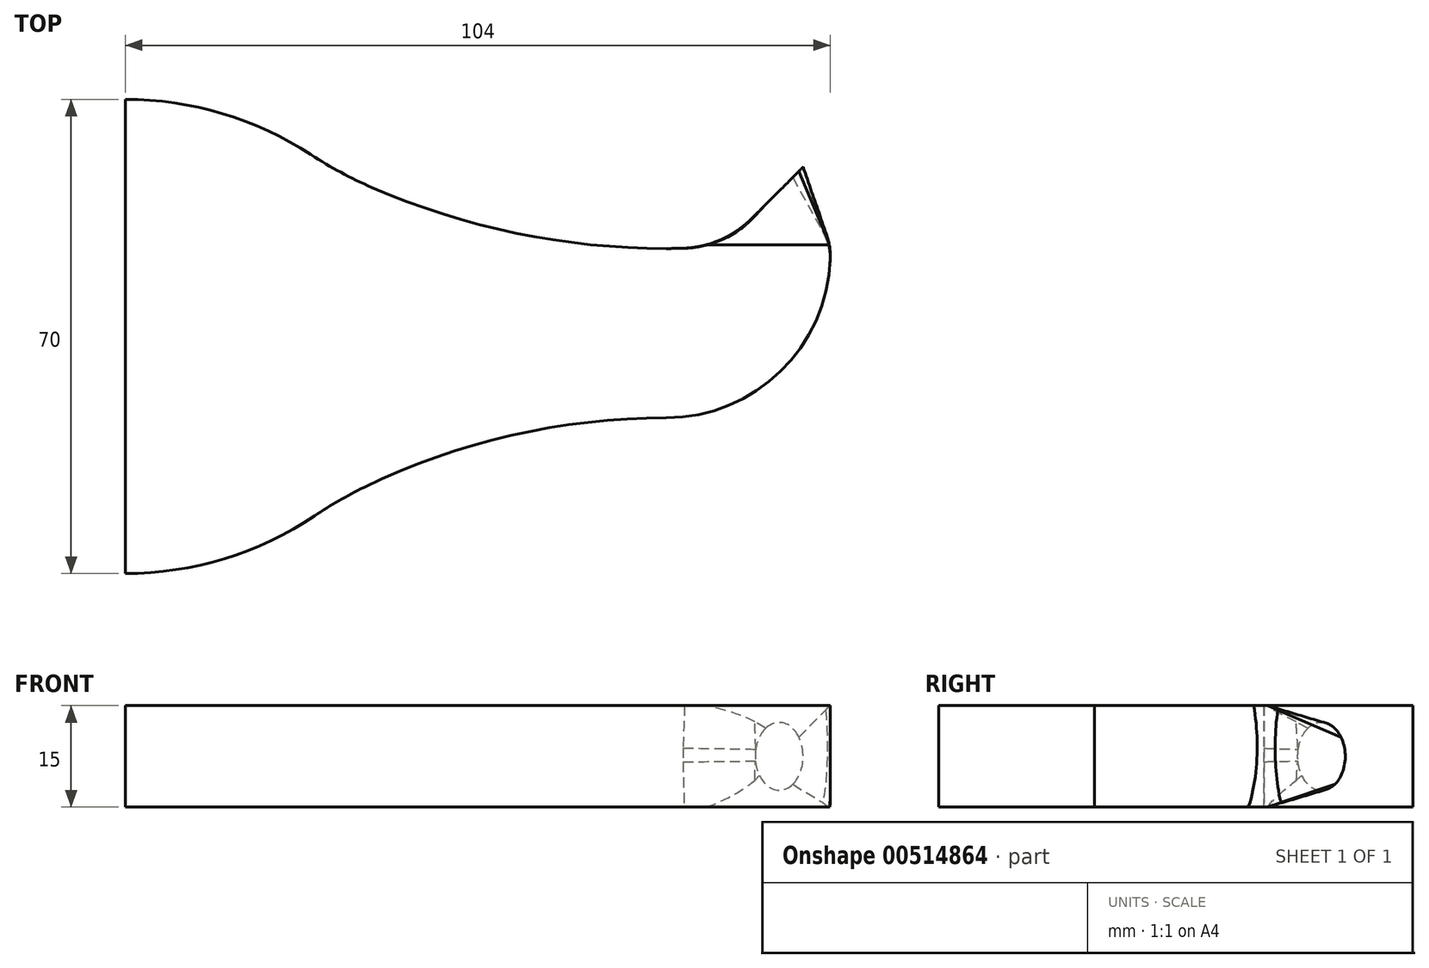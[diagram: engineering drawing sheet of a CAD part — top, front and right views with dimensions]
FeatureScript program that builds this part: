
annotation { "Feature Type Name" : "Feature", "Feature Type Description" : "" }
export const myFeature = defineFeature(function(context is Context, id is Id, definition is map)
    precondition{}
    {
        {
            var Q0;
            Q0=qCreatedBy(makeId("Top.planeOp"),FACE);
            var sketch = newSketch(context, id + "F0", { "sketchPlane" : qUnion([Q0])});
            skLineSegment(sketch, "E0.left", {"start": v(-50, 50) * mm, "end": v(-50, -50) * mm});
            skPoint(sketch, "E0.middle", {"position": v(0, 0) * mm});
            skLineSegment(sketch, "E1", {"start": v(-50, 50) * mm, "end": v(-50, 40) * mm});
            skLineSegment(sketch, "E2", {"start": v(50, 40) * mm, "end": v(42.93, 32.93) * mm});
            skLineSegment(sketch, "E3", {"start": v(42.93, 32.93) * mm, "end": v(46.46, 36.46) * mm});
            skLineSegment(sketch, "E4", {"start": v(-50, 0) * mm, "end": v(-50, -10) * mm});
            skLineSegment(sketch, "E5", {"start": v(-50, -10) * mm, "end": v(-50, 15) * mm});
            skLineSegment(sketch, "E6", {"start": v(-50, 15) * mm, "end": v(114.78, 15) * mm});
            skLineSegment(sketch, "E7", {"start": v(42.93, 32.93) * mm, "end": v(42.93, -37.04) * mm});
            skLineSegment(sketch, "E8", {"start": v(-50, 15) * mm, "end": v(30, 15) * mm});
            skLineSegment(sketch, "E9", {"start": v(30, 15) * mm, "end": v(30, 30) * mm});
            skLineSegment(sketch, "E10", {"start": v(30, 15) * mm, "end": v(30, 0) * mm});
            skLineSegment(sketch, "E11", {"start": v(42.93, 32.93) * mm, "end": v(81, 32.93) * mm});
            skLineSegment(sketch, "E12", {"start": v(46.46, 36.46) * mm, "end": v(46.46, 32.93) * mm});
            skLineSegment(sketch, "E13", {"start": v(46.46, 36.46) * mm, "end": v(46.46, 0) * mm});
            skLineSegment(sketch, "E14", {"start": v(46.46, 36.46) * mm, "end": v(62.14, 20.79) * mm});
            skLineSegment(sketch, "E15", {"start": v(-50, 50) * mm, "end": v(-109.66, 50) * mm});
            skLineSegment(sketch, "E16", {"start": v(-50, 40) * mm, "end": v(-110.5, 40) * mm});
            skLineSegment(sketch, "E17", {"start": v(-50, 15) * mm, "end": v(-113.83, 15) * mm});
            skLineSegment(sketch, "E18", {"start": v(-50, 0) * mm, "end": v(-113, 0) * mm});
            skLineSegment(sketch, "E19", {"start": v(-50, -10) * mm, "end": v(-113, -10) * mm});
            skLineSegment(sketch, "E20", {"start": v(-50, -50) * mm, "end": v(-111.33, -50) * mm});
            skLineSegment(sketch, "E21", {"start": v(30, 30) * mm, "end": v(95.7, 30) * mm});
            skPoint(sketch, "E22", {"position": v(42.93, 30) * mm});
            skPoint(sketch, "E23", {"position": v(46.46, 30) * mm});
            skPoint(sketch, "E24", {"position": v(42.93, 28.5) * mm});
            skLineSegment(sketch, "E25", {"start": v(30, 15) * mm, "end": v(30, 7.5) * mm});
            skLineSegment(sketch, "E26", {"start": v(30, 15) * mm, "end": v(30, 22.5) * mm});
            skLineSegment(sketch, "E27", {"start": v(30, 15) * mm, "end": v(0, 15) * mm});
            skLineSegment(sketch, "E28", {"start": v(-50, 15) * mm, "end": v(-30, 15) * mm});
            skLineSegment(sketch, "E29", {"start": v(-30, 15) * mm, "end": v(-10, 15) * mm});
            skLineSegment(sketch, "E30", {"start": v(-10, 15) * mm, "end": v(10, 15) * mm});
            skLineSegment(sketch, "E31", {"start": v(30, 30) * mm, "end": v(-50, 30) * mm});
            skLineSegment(sketch, "E32", {"start": v(-50, 40) * mm, "end": v(50, 40) * mm});
            skSolve(sketch);
        }
        {
            var Q0;
            Q0=sQuery(id+"F0.wireOp",EDGE,"E2");
            cPlane(context, id + "F1", {"entities" : qUnion([Q0]), "cplaneType" : CPlaneType.LINE_ANGLE, "offset" : 25 * mm, "angle" : 90 * degree, "width" : 150 * mm, "height" : 150 * mm});
        }
        {
            var Q0;
            Q0=qCreatedBy(id+"F1.planeOp",FACE);
            var sketch = newSketch(context, id + "F2", { "sketchPlane" : qUnion([Q0])});
            skCircle(sketch, "E33", {"center": v(58.64, 0) * mm, "radius": 5 * mm});
            skSolve(sketch);
        }
        {
            var Q0;
            Q0=sQuery(id+"F0.wireOp",VERTEX,"E6.start");
            var Q1;
            Q1=qCreatedBy(makeId("Right.planeOp"),FACE);
            cPlane(context, id + "F3", {"entities" : qUnion([Q0, Q1]), "cplaneType" : CPlaneType.PLANE_POINT, "offset" : 25 * mm, "width" : 150 * mm, "height" : 150 * mm});
        }
        {
            var Q0;
            Q0=qCreatedBy(id+"F3.planeOp",FACE);
            var sketch = newSketch(context, id + "F4", { "sketchPlane" : qUnion([Q0])});
            skPoint(sketch, "E34", {"position": v(15, 0) * mm});
            skLineSegment(sketch, "E35", {"start": v(50, 10) * mm, "end": v(-20, 10) * mm});
            skLineSegment(sketch, "E36", {"start": v(50, -10) * mm, "end": v(-20, -10) * mm});
            skLineSegment(sketch, "E37", {"start": v(50, 10) * mm, "end": v(50, -10) * mm});
            skLineSegment(sketch, "E38", {"start": v(-20, 10) * mm, "end": v(-20, -10) * mm});
            skPoint(sketch, "E39", {"position": v(-50, 0) * mm});
            skPoint(sketch, "E40", {"position": v(50, 0) * mm});
            skPoint(sketch, "E41", {"position": v(-20, 0) * mm});
            skLineSegment(sketch, "E42", {"start": v(50, 0) * mm, "end": v(40, 0) * mm});
            skSolve(sketch);
        }
        {
            var Q0;
            Q0=qCreatedBy(makeId("Front.planeOp"),FACE);
            var Q1;
            Q1=sQuery(id+"F0.wireOp",VERTEX,"E24");
            cPlane(context, id + "F5", {"entities" : qUnion([Q0, Q1]), "cplaneType" : CPlaneType.PLANE_POINT, "offset" : 25 * mm, "width" : 150 * mm, "height" : 150 * mm});
        }
        {
            var Q0;
            Q0=qCreatedBy(id+"F5.planeOp",FACE);
            var sketch = newSketch(context, id + "F6", { "sketchPlane" : qUnion([Q0])});
            skPoint(sketch, "E43", {"position": v(46.46, 0) * mm});
            skLineSegment(sketch, "E44.bottom", {"start": v(38.96, -7.5) * mm, "end": v(53.96, -7.5) * mm});
            skLineSegment(sketch, "E44.top", {"start": v(38.96, 7.5) * mm, "end": v(53.96, 7.5) * mm});
            skLineSegment(sketch, "E44.left", {"start": v(38.96, -7.5) * mm, "end": v(38.96, 7.5) * mm});
            skLineSegment(sketch, "E44.right", {"start": v(53.96, -7.5) * mm, "end": v(53.96, 7.5) * mm});
            skPoint(sketch, "E45", {"position": v(38.96, 0) * mm});
            skPoint(sketch, "E46", {"position": v(53.96, 0) * mm});
            skSolve(sketch);
        }
        {
            var Q0;
            Q0=qCreatedBy(makeId("Top.planeOp"),FACE);
            var Q1;
            Q1=sQuery(id+"F6.wireOp",VERTEX,"E43");
            cPlane(context, id + "F7", {"entities" : qUnion([Q0, Q1]), "cplaneType" : CPlaneType.PLANE_POINT, "offset" : 25 * mm, "width" : 150 * mm, "height" : 150 * mm});
        }
        {
            var Q0;
            Q0=qCreatedBy(id+"F7.planeOp",FACE);
            var sketch = newSketch(context, id + "F8", { "sketchPlane" : qUnion([Q0])});
            skPoint(sketch, "E47", {"position": v(29.78, 27.97) * mm});
            skPoint(sketch, "E48", {"position": v(29.78, 2.97) * mm});
            skLineSegment(sketch, "E49", {"start": v(29.78, 27.97) * mm, "end": v(29.78, 2.97) * mm});
            skLineSegment(sketch, "E50", {"start": v(29.78, 27.97) * mm, "end": v(25.89, 27.97) * mm});
            skLineSegment(sketch, "E51", {"start": v(29.78, 2.97) * mm, "end": v(25.8, 2.97) * mm});
            skPoint(sketch, "E52", {"position": v(29.78, 15.47) * mm});
            skPoint(sketch, "E53", {"position": v(38.96, 28.5) * mm});
            skPoint(sketch, "E54", {"position": v(53.96, 28.5) * mm});
            skArc(sketch, "E55", {"start": v(29.78, 27.97) * mm, "mid": v(34.38, 28.1) * mm, "end": v(38.96, 28.5) * mm});
            skArc(sketch, "E56", {"start": v(29.78, 2.97) * mm, "mid": v(47.36, 10.54) * mm, "end": v(53.96, 28.5) * mm});
            skLineSegment(sketch, "E57", {"start": v(38.96, 28.5) * mm, "end": v(53.96, 28.5) * mm});
            skLineSegment(sketch, "E58", {"start": v(29.78, 15.47) * mm, "end": v(-60.44, 15.47) * mm});
            skSolve(sketch);
        }
        {
            var Q0;
            Q0=qCreatedBy(makeId("Top.planeOp"),FACE);
            var sketch = newSketch(context, id + "F9", { "sketchPlane" : qUnion([Q0])});
            skLineSegment(sketch, "E59", {"start": v(-20, 40) * mm, "end": v(-20, 40) * mm});
            skPoint(sketch, "E60", {"position": v(-50, -50) * mm});
            skPoint(sketch, "E61", {"position": v(29.78, 2.97) * mm});
            skPoint(sketch, "E62", {"position": v(29.78, 27.97) * mm});
            skLineSegment(sketch, "E63", {"start": v(29.78, 27.97) * mm, "end": v(24.78, 27.97) * mm});
            skLineSegment(sketch, "E64", {"start": v(29.78, 2.97) * mm, "end": v(24.78, 2.97) * mm});
            skArc(sketch, "E65", {"start": v(-20, 40) * mm, "mid": v(4.18, 31.02) * mm, "end": v(29.78, 27.97) * mm});
            skLineSegment(sketch, "E66", {"start": v(29.78, 27.97) * mm, "end": v(29.78, 2.97) * mm});
            skLineSegment(sketch, "E67", {"start": v(29.78, 15.47) * mm, "end": v(16.82, 15.47) * mm});
            skPoint(sketch, "E68", {"position": v(-50, 50) * mm});
            skPoint(sketch, "E69", {"position": v(-50, -20) * mm});
            skPoint(sketch, "E70", {"position": v(-50, 15.47) * mm});
            skLineSegment(sketch, "E71", {"start": v(-50, 50) * mm, "end": v(-50, -20) * mm});
            skLineSegment(sketch, "E72", {"start": v(-50, 50) * mm, "end": v(-61.71, 50) * mm});
            skArc(sketch, "E73", {"start": v(-20, 40) * mm, "mid": v(-34.19, 47.43) * mm, "end": v(-50, 50) * mm});
            skArc(sketch, "E74.MirrorCS", {"start": v(-20, -10) * mm, "mid": v(-34.19, -17.43) * mm, "end": v(-50, -20) * mm});
            skLineSegment(sketch, "E75", {"start": v(29.78, 2.97) * mm, "end": v(35.09, 2.97) * mm});
            skArc(sketch, "E76", {"start": v(29.78, 2.97) * mm, "mid": v(4.06, -0.32) * mm, "end": v(-20, -10) * mm});
            skSolve(sketch);
        }
        {
            var Q0;
            Q0=makeQuery(id+"F2.imprint","IMPRINT",FACE,{"disambiguationData":[TD([[makeQuery(id+"F2.imprint","IMPRINT",EDGE,{"derivedFrom":sQuery(id+"F2.wireOp",EDGE,"E33")}),1.0]])]});
            var Q1;
            Q1=makeQuery(id+"F6.imprint","IMPRINT",FACE,{"disambiguationData":[TD([[makeQuery(id+"F6.imprint","IMPRINT",EDGE,{"derivedFrom":sQuery(id+"F6.wireOp",EDGE,"E44.bottom")}),1.0]])]});
            loft(context, id + "F10", {"sheetProfilesArray" : [{ "sheetProfileEntities" : qUnion([Q0]) }, { "sheetProfileEntities" : qUnion([Q1]) }]});
        }
        {
            var Q0;
            {var subQ1=sQuery(id+"F9.wireOp",EDGE,"E65");Q0=makeQuery(id+"F9.imprint","IMPRINT",FACE,{"disambiguationData":[TD([[makeQuery(id+"F9.imprint","IMPRINT",EDGE,{"derivedFrom":subQ1}),-1.0]])]});}
            extrude(context, id + "F11", {"entities" : qUnion([Q0]), "operationType" : NewBodyOperationType.ADD, "endBound" : BoundingType.SYMMETRIC, "depth" : 15 * mm, "offsetDistance" : 25 * mm});
        }
        {
            var Q0;
            Q0=makeQuery(id+"F8.imprint","IMPRINT",FACE,{"disambiguationData":[TD([[makeQuery(id+"F8.imprint","IMPRINT",EDGE,{"derivedFrom":sQuery(id+"F8.wireOp",EDGE,"E49")}),1.0]])]});
            extrude(context, id + "F12", {"entities" : qUnion([Q0]), "operationType" : NewBodyOperationType.ADD, "endBound" : BoundingType.SYMMETRIC, "depth" : 15 * mm, "offsetDistance" : 25 * mm});
        }
        {
            var Q0;
            Q0=makeQuery(id+"F12.boolean.opBoolean","MERGE",EDGE,{"derivedFrom":[makeQuery(id+"F10.opLoft","MID_CAP_EDGE",EDGE,{"disambiguationData":[OSD([sQuery(id+"F6.wireOp",EDGE,"E44.bottom"),sQuery(id+"F6.wireOp",EDGE,"E44.top"),sQuery(id+"F6.wireOp",EDGE,"E44.left")])],"capPos":1.0}),makeQuery(id+"F12.opExtrude","SWEPT_EDGE",EDGE,{"disambiguationData":[OSD([sQuery(id+"F8.wireOp",EDGE,"E55"),sQuery(id+"F8.wireOp",EDGE,"E57")])]})]});
            fillet(context, id + "F13", {"entities" : qUnion([Q0]), "radius" : 15 * mm, "tangentPropagation" : true, "allowEdgeOverflow" : false});
        }
        {
            var Q0;
            Q0=makeQuery(id+"F12.boolean.opBoolean","MERGE",EDGE,{"derivedFrom":[makeQuery(id+"F10.opLoft","MID_CAP_EDGE",EDGE,{"disambiguationData":[OSD([sQuery(id+"F6.wireOp",EDGE,"E44.bottom"),sQuery(id+"F6.wireOp",EDGE,"E44.top"),sQuery(id+"F6.wireOp",EDGE,"E44.right")])],"capPos":1.0}),makeQuery(id+"F12.opExtrude","SWEPT_EDGE",EDGE,{"disambiguationData":[OSD([sQuery(id+"F8.wireOp",EDGE,"E56"),sQuery(id+"F8.wireOp",EDGE,"E57")])]})]});
            fillet(context, id + "F14", {"entities" : qUnion([Q0]), "radius" : 8 * mm, "tangentPropagation" : true, "allowEdgeOverflow" : false});
        }
        {
            var Q0;
            Q0=makeQuery(id+"F11.opExtrude","SWEPT_EDGE",EDGE,{"disambiguationData":[OSD([sQuery(id+"F9.wireOp",EDGE,"E65"),sQuery(id+"F9.wireOp",EDGE,"E73")])]});
            fillet(context, id + "F15", {"entities" : qUnion([Q0]), "radius" : 60 * mm, "tangentPropagation" : true, "allowEdgeOverflow" : false});
        }
        {
            var Q0;
            Q0=makeQuery(id+"F11.opExtrude","SWEPT_EDGE",EDGE,{"disambiguationData":[OSD([sQuery(id+"F9.wireOp",EDGE,"E74.MirrorCS"),sQuery(id+"F9.wireOp",EDGE,"E76")])]});
            fillet(context, id + "F16", {"entities" : qUnion([Q0]), "radius" : 60 * mm, "tangentPropagation" : true, "allowEdgeOverflow" : false});
        }
        {
            var Q0;
            Q0=qCreatedBy(makeId("Right.planeOp"),FACE);
            var Q1;
            Q1=sQuery(id+"F4.wireOp",VERTEX,"E34");
            cPlane(context, id + "F17", {"entities" : qUnion([Q0, Q1]), "cplaneType" : CPlaneType.PLANE_POINT, "offset" : 25 * mm, "width" : 150 * mm, "height" : 150 * mm});
        }
        {
            var Q0;
            Q0=qCreatedBy(id+"F1.planeOp",FACE);
            var Q1;
            Q1=sQuery(id+"F2.wireOp",VERTEX,"E33.center");
            cPlane(context, id + "F18", {"entities" : qUnion([Q0, Q1]), "cplaneType" : CPlaneType.PLANE_POINT, "offset" : 25 * mm, "width" : 150 * mm, "height" : 150 * mm});
        }
        {
            var Q0;
            Q0=qCreatedBy(id+"F18.planeOp",FACE);
            var sketch = newSketch(context, id + "F19", { "sketchPlane" : qUnion([Q0])});
            skCircle(sketch, "E77", {"center": v(58.64, 0) * mm, "radius": 5 * mm});
            skPoint(sketch, "E78", {"position": v(63.64, 0) * mm});
            skSolve(sketch);
        }
        {
            var Q0;
            Q0=sQuery(id+"F0.wireOp",VERTEX,"E27.end");
            var Q1;
            Q1=qCreatedBy(makeId("Top.planeOp"),FACE);
            cPlane(context, id + "F20", {"entities" : qUnion([Q0, Q1]), "cplaneType" : CPlaneType.PLANE_POINT, "offset" : 25 * mm, "width" : 150 * mm, "height" : 150 * mm});
        }
        {
            var Q0;
            Q0=sQuery(id+"F19.wireOp",VERTEX,"E77.center");
            var Q1;
            Q1=qCreatedBy(id+"F3.planeOp",FACE);
            cPlane(context, id + "F21", {"entities" : qUnion([Q0, Q1]), "cplaneType" : CPlaneType.PLANE_POINT, "offset" : 25 * mm, "width" : 150 * mm, "height" : 150 * mm});
        }
    });
